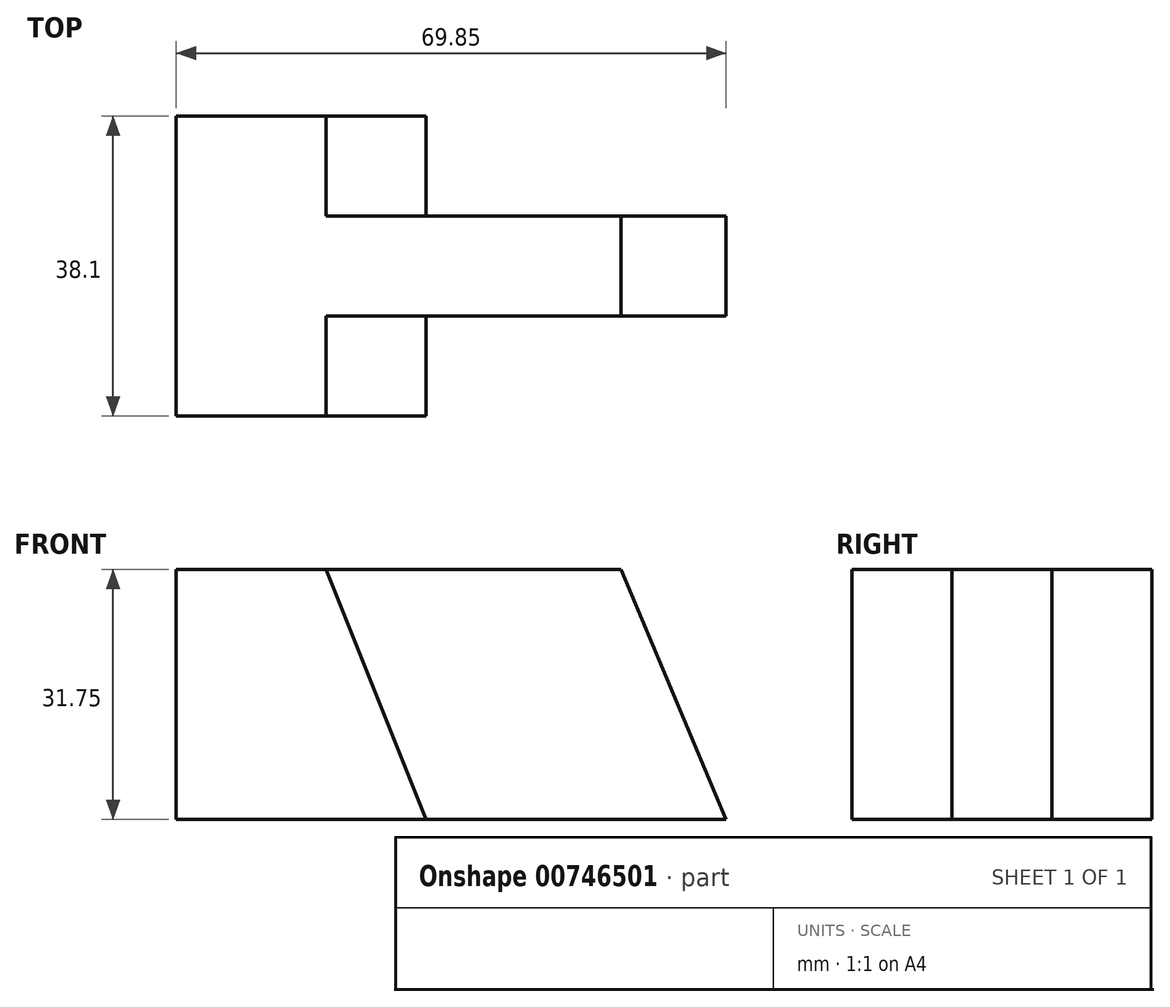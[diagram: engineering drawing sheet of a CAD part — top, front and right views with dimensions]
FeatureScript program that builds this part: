
annotation { "Feature Type Name" : "Feature", "Feature Type Description" : "" }
export const myFeature = defineFeature(function(context is Context, id is Id, definition is map)
    precondition{}
    {
        {
            var Q0;
            Q0=qCreatedBy(makeId("Top.planeOp"),FACE);
            var sketch = newSketch(context, id + "F0", { "sketchPlane" : qUnion([Q0])});
            skLineSegment(sketch, "E0", {"start": v(0, 0) * mm, "end": v(0, 38.1) * mm});
            skLineSegment(sketch, "E1", {"start": v(0, 38.1) * mm, "end": v(31.75, 38.1) * mm});
            skLineSegment(sketch, "E2", {"start": v(31.75, 38.1) * mm, "end": v(31.75, 25.4) * mm});
            skLineSegment(sketch, "E3", {"start": v(31.75, 25.4) * mm, "end": v(69.85, 25.4) * mm});
            skLineSegment(sketch, "E4", {"start": v(69.85, 25.4) * mm, "end": v(69.85, 12.7) * mm});
            skLineSegment(sketch, "E5", {"start": v(69.85, 12.7) * mm, "end": v(31.75, 12.7) * mm});
            skLineSegment(sketch, "E6", {"start": v(31.75, 12.7) * mm, "end": v(31.75, 0) * mm});
            skLineSegment(sketch, "E7", {"start": v(31.75, 0) * mm, "end": v(0, 0) * mm});
            skSolve(sketch);
        }
        {
            var Q0;
            Q0=makeQuery(id+"F0.imprint","IMPRINT",FACE,{"disambiguationData":[TD([[makeQuery(id+"F0.imprint","IMPRINT",EDGE,{"derivedFrom":sQuery(id+"F0.wireOp",EDGE,"E0")}),-1.0]])]});
            extrude(context, id + "F1", {"entities" : qUnion([Q0]), "depth" : 31.75 * mm, "offsetDistance" : 25.4 * mm});
        }
        {
            var Q0;
            Q0=makeQuery(id+"F1.opExtrude","SWEPT_FACE",FACE,{"disambiguationData":[OSD([sQuery(id+"F0.wireOp",EDGE,"E5")])]});
            var sketch = newSketch(context, id + "F2", { "sketchPlane" : qUnion([Q0])});
            skLineSegment(sketch, "E8", {"start": v(56.5, 31.75) * mm, "end": v(69.85, 0) * mm});
            skLineSegment(sketch, "E9", {"start": v(69.85, 0) * mm, "end": v(69.85, 31.75) * mm});
            skLineSegment(sketch, "E10", {"start": v(69.2, 31.9) * mm, "end": v(56.5, 31.75) * mm});
            skSolve(sketch);
        }
        {
            var Q0;
            {var subQ0=sQuery(id+"F2.wireOp",EDGE,"E8");Q0=makeQuery(id+"F2.imprint","IMPRINT",FACE,{"disambiguationData":[TD([[makeQuery(id+"F2.imprint","IMPRINT",EDGE,{"derivedFrom":subQ0}),1.0]])]});}
            extrude(context, id + "F3", {"entities" : qUnion([Q0]), "operationType" : NewBodyOperationType.REMOVE, "oppositeDirection" : true, "depth" : 25.4 * mm, "offsetDistance" : 25.4 * mm});
        }
        {
            var Q0;
            Q0=makeQuery(id+"F1.opExtrude","SWEPT_FACE",FACE,{"disambiguationData":[OSD([sQuery(id+"F0.wireOp",EDGE,"E7")])]});
            var sketch = newSketch(context, id + "F4", { "sketchPlane" : qUnion([Q0])});
            skLineSegment(sketch, "E11", {"start": v(19.05, 31.75) * mm, "end": v(31.75, 0) * mm});
            skLineSegment(sketch, "E12", {"start": v(31.75, 0) * mm, "end": v(31.75, 31.75) * mm});
            skLineSegment(sketch, "E13", {"start": v(31.75, 31.75) * mm, "end": v(19.05, 31.75) * mm});
            skSolve(sketch);
        }
        {
            var Q0;
            Q0=makeQuery(id+"F4.imprint","IMPRINT",FACE,{"disambiguationData":[TD([[makeQuery(id+"F4.imprint","IMPRINT",EDGE,{"derivedFrom":sQuery(id+"F4.wireOp",EDGE,"E11")}),1.0]])]});
            extrude(context, id + "F5", {"entities" : qUnion([Q0]), "operationType" : NewBodyOperationType.REMOVE, "oppositeDirection" : true, "depth" : 12.7 * mm, "offsetDistance" : 25.4 * mm});
        }
        {
            var Q0;
            Q0=makeQuery(id+"F1.opExtrude","SWEPT_FACE",FACE,{"disambiguationData":[OSD([sQuery(id+"F0.wireOp",EDGE,"E1")])]});
            var sketch = newSketch(context, id + "F6", { "sketchPlane" : qUnion([Q0])});
            skLineSegment(sketch, "E14", {"start": v(-31.75, 0) * mm, "end": v(-19.05, 31.75) * mm});
            skLineSegment(sketch, "E15", {"start": v(-19.05, 31.75) * mm, "end": v(-31.75, 31.75) * mm});
            skLineSegment(sketch, "E16", {"start": v(-31.75, 31.75) * mm, "end": v(-31.75, 0) * mm});
            skSolve(sketch);
        }
        {
            var Q0;
            Q0=makeQuery(id+"F6.imprint","IMPRINT",FACE,{"disambiguationData":[TD([[makeQuery(id+"F6.imprint","IMPRINT",EDGE,{"derivedFrom":sQuery(id+"F6.wireOp",EDGE,"E14")}),1.0]])]});
            extrude(context, id + "F7", {"entities" : qUnion([Q0]), "operationType" : NewBodyOperationType.REMOVE, "oppositeDirection" : true, "depth" : 12.7 * mm, "offsetDistance" : 25.4 * mm});
        }
    });
